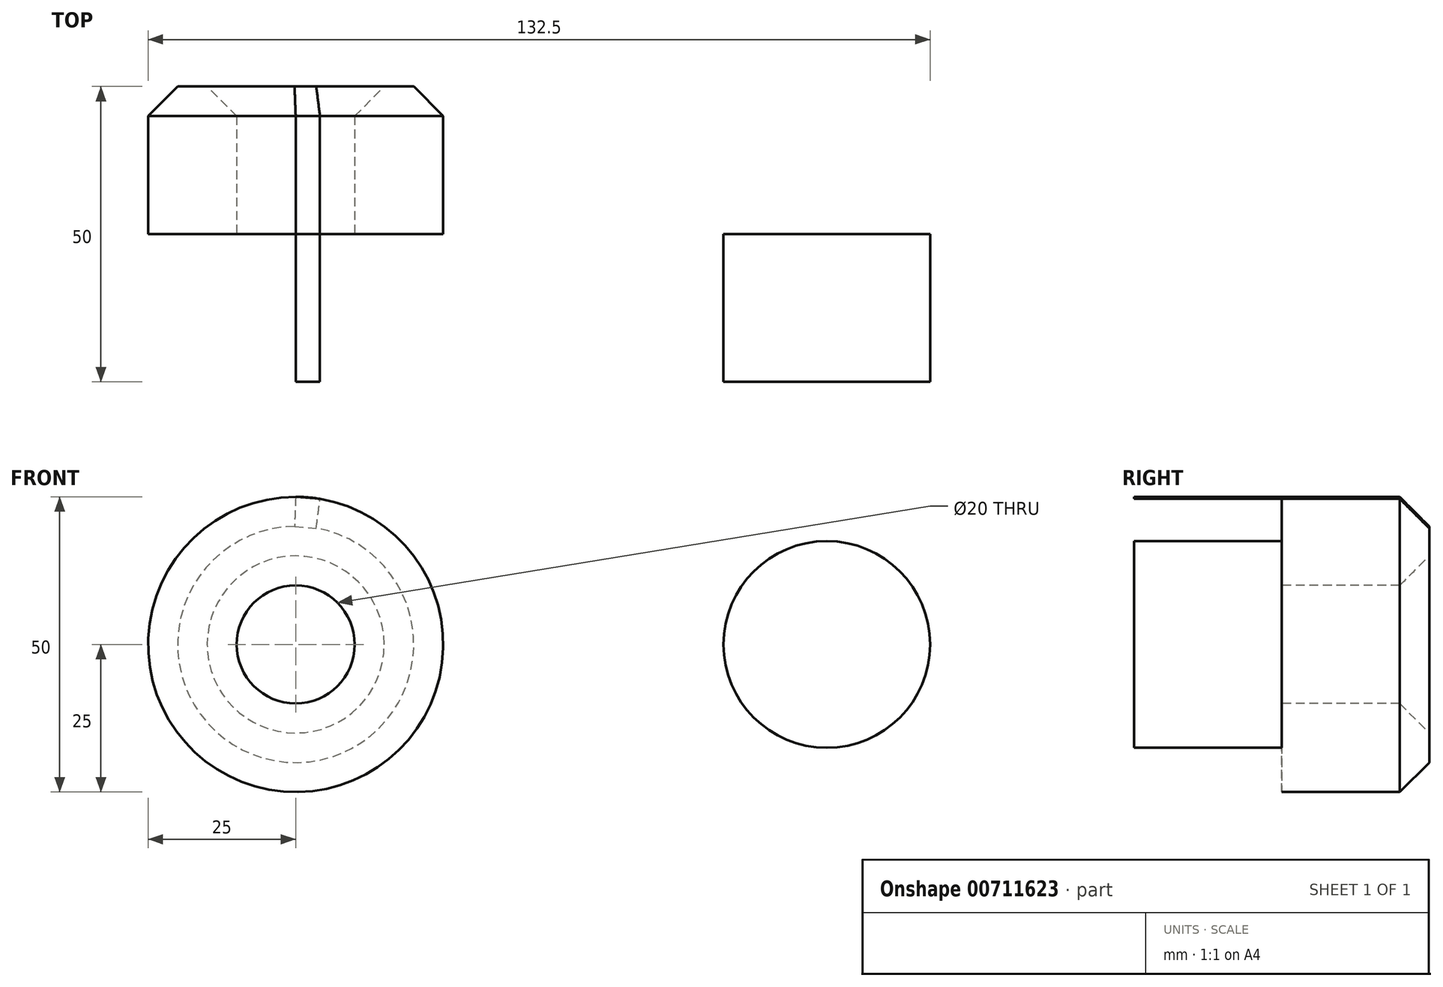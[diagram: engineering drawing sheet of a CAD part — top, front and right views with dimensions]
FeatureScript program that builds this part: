
annotation { "Feature Type Name" : "Feature", "Feature Type Description" : "" }
export const myFeature = defineFeature(function(context is Context, id is Id, definition is map)
    precondition{}
    {
        {
            var Q0;
            Q0=qCreatedBy(makeId("Front.planeOp"),FACE);
            var sketch = newSketch(context, id + "F0", { "sketchPlane" : qUnion([Q0])});
            skCircle(sketch, "E0", {"center": v(0, 0) * mm, "radius": 25 * mm});
            skCircle(sketch, "E1", {"center": v(90, 0) * mm, "radius": 17.5 * mm});
            skLineSegment(sketch, "E2", {"start": v(0, 25) * mm, "end": v(91.44, 17.44) * mm});
            skLineSegment(sketch, "E3", {"start": v(0, -25) * mm, "end": v(91.44, -17.44) * mm});
            skSolve(sketch);
        }
        {
            var Q0;
            {var subQ0=sQuery(id+"F0.wireOp",EDGE,"E2");var subQ1=sQuery(id+"F0.wireOp",EDGE,"E0");var subQ2=makeQuery(id+"F0.imprint","INTERSECT",VERTEX,{"disambiguationData":[OD(1.0)],"derivedFrom":[subQ1,subQ0]});Q0=makeQuery(id+"F0.imprint","IMPRINT",FACE,{"disambiguationData":[TD([[makeQuery(id+"F0.imprint","IMPRINT",EDGE,{"disambiguationData":[TD([[subQ2,1.0]])],"derivedFrom":subQ1}),-1.0]])]});}
            var Q1;
            {var subQ0=sQuery(id+"F0.wireOp",EDGE,"E1");var subQ1=makeQuery(id+"F0.imprint","INTERSECT",VERTEX,{"derivedFrom":[subQ0,sQuery(id+"F0.wireOp",EDGE,"E2")]});Q1=makeQuery(id+"F0.imprint","IMPRINT",FACE,{"disambiguationData":[TD([[makeQuery(id+"F0.imprint","IMPRINT",EDGE,{"disambiguationData":[TD([[subQ1,-1.0]])],"derivedFrom":subQ0}),1.0]])]});}
            var Q2;
            {var subQ0=sQuery(id+"F0.wireOp",EDGE,"E2");var subQ1=sQuery(id+"F0.wireOp",EDGE,"E0");var subQ2=makeQuery(id+"F0.imprint","INTERSECT",VERTEX,{"disambiguationData":[OD(0.0)],"derivedFrom":[subQ1,subQ0]});Q2=makeQuery(id+"F0.imprint","IMPRINT",FACE,{"disambiguationData":[TD([[makeQuery(id+"F0.imprint","IMPRINT",EDGE,{"disambiguationData":[TD([[subQ2,-1.0]])],"derivedFrom":subQ1}),1.0]])]});}
            extrude(context, id + "F1", {"entities" : qUnion([Q0, Q1, Q2]), "depth" : 25 * mm, "offsetDistance" : 25 * mm});
        }
        {
            var Q0;
            Q0=makeQuery(id+"F1.opExtrude","CAP_FACE",FACE,{"disambiguationData":[OSD([sQuery(id+"F0.wireOp",EDGE,"E0"),sQuery(id+"F0.wireOp",EDGE,"E1"),sQuery(id+"F0.wireOp",EDGE,"E2"),sQuery(id+"F0.wireOp",EDGE,"E3")])],"isStart":true});
            var sketch = newSketch(context, id + "F2", { "sketchPlane" : qUnion([Q0])});
            skCircle(sketch, "E4", {"center": v(0, 0) * mm, "radius": 25 * mm});
            skCircle(sketch, "E5", {"center": v(0, 0) * mm, "radius": 10 * mm});
            skCircle(sketch, "E6", {"center": v(-90, 0) * mm, "radius": 10 * mm});
            skSolve(sketch);
        }
        {
            var Q0;
            Q0=makeQuery(id+"F2.imprint","IMPRINT",FACE,{"disambiguationData":[TD([[makeQuery(id+"F2.imprint","IMPRINT",EDGE,{"derivedFrom":sQuery(id+"F2.wireOp",EDGE,"E5")}),-1.0]])]});
            extrude(context, id + "F3", {"entities" : qUnion([Q0]), "operationType" : NewBodyOperationType.ADD, "depth" : 25 * mm, "offsetDistance" : 25 * mm});
        }
        {
            var Q0;
            {var subQ0=sQuery(id+"F2.wireOp",EDGE,"E4");Q0=makeQuery(id+"F3.opExtrude","CAP_EDGE",EDGE,{"disambiguationData":[OSD([subQ0]),TDD([makeQuery(id+"F2.imprint","IMPRINT",EDGE,{"disambiguationData":[TD([[makeQuery(id+"F2.imprint","INTERSECT",VERTEX,{"disambiguationData":[OD(1.0)],"derivedFrom":[makeQuery(id+"F1.opExtrude","CAP_EDGE",EDGE,{"disambiguationData":[OSD([sQuery(id+"F0.wireOp",EDGE,"E2")])],"isStart":true}),subQ0]}),-1.0],[makeQuery(id+"F2.imprint","INTERSECT",VERTEX,{"disambiguationData":[OD(1.0)],"derivedFrom":[makeQuery(id+"F1.opExtrude","CAP_EDGE",EDGE,{"disambiguationData":[OSD([sQuery(id+"F0.wireOp",EDGE,"E3")])],"isStart":true}),subQ0]}),1.0]])],"derivedFrom":subQ0})])],"isStart":false});}
            var Q1;
            {var subQ0=sQuery(id+"F2.wireOp",EDGE,"E4");Q1=makeQuery(id+"F3.opExtrude","CAP_EDGE",EDGE,{"disambiguationData":[OSD([subQ0]),TDD([makeQuery(id+"F2.imprint","IMPRINT",EDGE,{"disambiguationData":[TD([[makeQuery(id+"F2.imprint","INTERSECT",VERTEX,{"disambiguationData":[OD(0.0)],"derivedFrom":[makeQuery(id+"F1.opExtrude","CAP_EDGE",EDGE,{"disambiguationData":[OSD([sQuery(id+"F0.wireOp",EDGE,"E2")])],"isStart":true}),subQ0]}),-1.0],[makeQuery(id+"F2.imprint","INTERSECT",VERTEX,{"disambiguationData":[OD(0.0)],"derivedFrom":[makeQuery(id+"F1.opExtrude","CAP_EDGE",EDGE,{"disambiguationData":[OSD([sQuery(id+"F0.wireOp",EDGE,"E3")])],"isStart":true}),subQ0]}),1.0]])],"derivedFrom":subQ0})])],"isStart":false});}
            var Q2;
            Q2=makeQuery(id+"F3.opExtrude","CAP_EDGE",EDGE,{"disambiguationData":[OSD([sQuery(id+"F0.wireOp",EDGE,"E2")])],"isStart":false});
            var Q3;
            Q3=makeQuery(id+"F3.opExtrude","CAP_EDGE",EDGE,{"disambiguationData":[OSD([sQuery(id+"F0.wireOp",EDGE,"E3")])],"isStart":false});
            var Q4;
            Q4=makeQuery(id+"F3.opExtrude","CAP_EDGE",EDGE,{"disambiguationData":[OSD([sQuery(id+"F2.wireOp",EDGE,"E5")])],"isStart":false});
            chamfer(context, id + "F4", {"entities" : qUnion([Q0, Q1, Q2, Q3, Q4]), "width" : 5 * mm, "tangentPropagation" : true});
        }
    });
